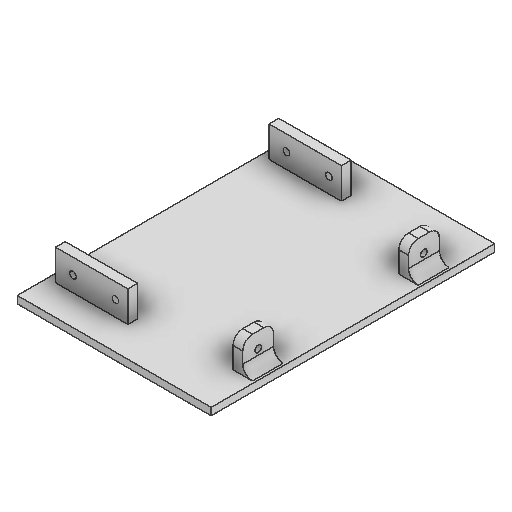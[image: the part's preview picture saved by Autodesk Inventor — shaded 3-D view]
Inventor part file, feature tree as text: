
AUTODESK INVENTOR PART (.ipt)
format: ipt  version: 2025 (Build 290162000, 162)  size: 210,432 bytes
history: native  units: mm
features: sketch x8, extrude x7, projected_geometry x6, other x6, reference x4, fillet x1, mirror x1
ambient origin geometry x8: Origin, YZ Plane, XZ Plane, XY Plane, X Axis, Y Axis, Z Axis, Center Point
bodies: Solid1 (feature_tree)
feature tree (33):
  extrude  "Extrusion1"  Depth=234.0mm
  extrude  "Extrusion2"  Depth=6.0mm
  extrude  "Extrusion3"  Depth=25.4mm TaperAngle=0.0deg
  fillet  "Fillet1"  Radius=1.0mm
  extrude  "Extrusion4"  Depth=25.4mm TaperAngle=0.0deg
  extrude  "Extrusion5"  Depth=8.0mm
  mirror  "Mirror1"
  extrude  "Extrusion6"  Depth=25.4mm
  extrude  "Extrusion7"  Depth=10.0mm
  sketch  "Sketch1"  dims[d0=160.0mm d1=234.0mm]
  sketch  "Sketch2"  dims[d5=8.0mm d6=25.4mm d7=0.0mm d8=1.0mm]
  projected_geometry  "Projected Loop1"
  reference  "Reference1"
  reference  "Reference2"
  sketch  "Sketch3"  dims[d9=5.5mm d10=25.4mm d11=0.0mm]
  projected_geometry  "Projected Loop2"
  sketch  "Sketch4"  dims[d12=8.0mm d14=8.0mm]
  projected_geometry  "Projected Loop3"
  reference  "Reference3"
  reference  "Reference4"
  sketch  "Sketch5"  dims[d15=25.4mm d16=0.0mm d17=5.5mm]
  projected_geometry  "Projected Loop4"
  sketch  "Sketch Rectangular Pattern1"  dims[d2=6.0mm d3=0.0mm d4=26.4mm]
  sketch  "Sketch6"  dims[d18=25.4mm d19=0.0mm d20=30.0mm d22=35.0mm d23=10.0mm d25=10.0mm]
  projected_geometry  "Projected Loop5"
  sketch  "Sketch7"  dims[d27=155.0mm d28=55.0mm d29=76.2mm d30=5.0mm d31=8.0mm d32=0.0mm d33=2.0mm d34=0.0mm]
  projected_geometry  "Projected Loop6"
  other  "<userpath>\Desktop\puppycat\woodhouseMK1.iam"
  other  "woodhouseMK1.iam"
  other  "lowerUndercarriageBracketFlipped:1"
  other  "horizontalStrutLower:1"
  other  "10inStrut:2"
  other  "4844N105_T-Slotted Framing Structural Bracket:1"
